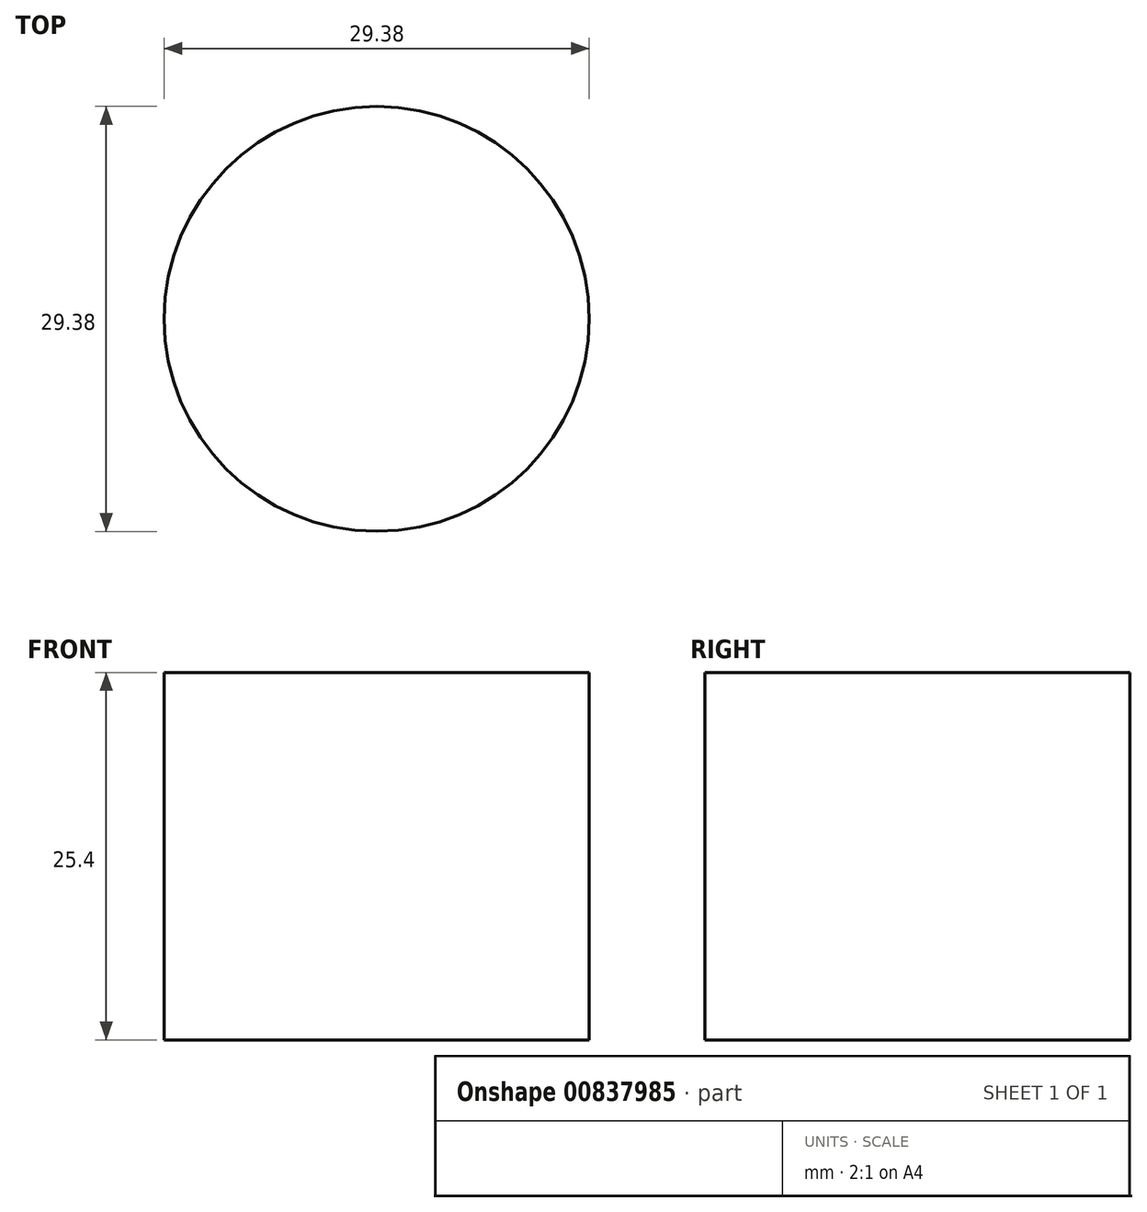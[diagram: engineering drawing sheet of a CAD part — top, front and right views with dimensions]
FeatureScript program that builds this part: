
annotation { "Feature Type Name" : "Feature", "Feature Type Description" : "" }
export const myFeature = defineFeature(function(context is Context, id is Id, definition is map)
    precondition{}
    {
        {
            var Q0;
            Q0=qCreatedBy(makeId("Top.planeOp"),FACE);
            var sketch = newSketch(context, id + "F0", { "sketchPlane" : qUnion([Q0])});
            skCircle(sketch, "E0", {"center": v(0, 0) * mm, "radius": 14.69 * mm});
            skSolve(sketch);
        }
        {
            var Q0;
            Q0 = qSketchRegion(id + "F0", true);
            extrude(context, id + "F1", {"entities" : qUnion([Q0]), "depth" : 25.4 * mm, "offsetDistance" : 25.4 * mm});
        }
    });
